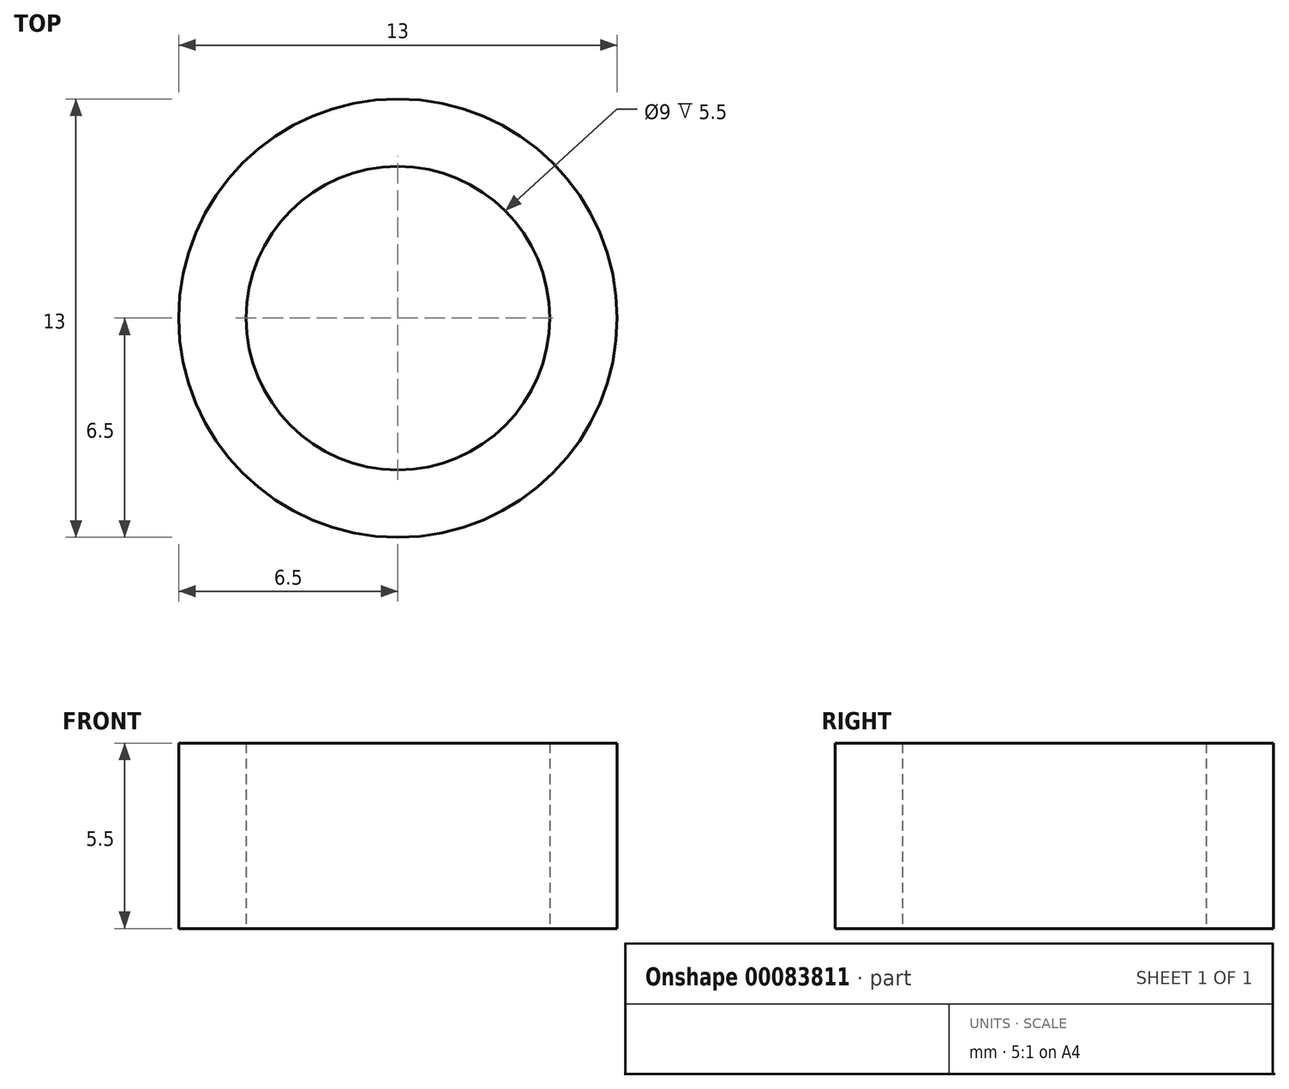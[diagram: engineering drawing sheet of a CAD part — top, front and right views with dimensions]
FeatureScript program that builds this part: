
annotation { "Feature Type Name" : "Feature", "Feature Type Description" : "" }
export const myFeature = defineFeature(function(context is Context, id is Id, definition is map)
    precondition{}
    {
        {
            var Q0;
            Q0=qCreatedBy(makeId("Top.planeOp"),FACE);
            var sketch = newSketch(context, id + "F0", { "sketchPlane" : qUnion([Q0])});
            skCircle(sketch, "E0", {"center": v(0, 0) * mm, "radius": 6.5 * mm});
            skCircle(sketch, "E1", {"center": v(0, 0) * mm, "radius": 4.5 * mm});
            skSolve(sketch);
        }
        {
            var Q0;
            Q0 = qSketchRegion(id + "F0", true);
            extrude(context, id + "F1", {"entities" : qUnion([Q0]), "depth" : 5.5 * mm});
        }
    });
